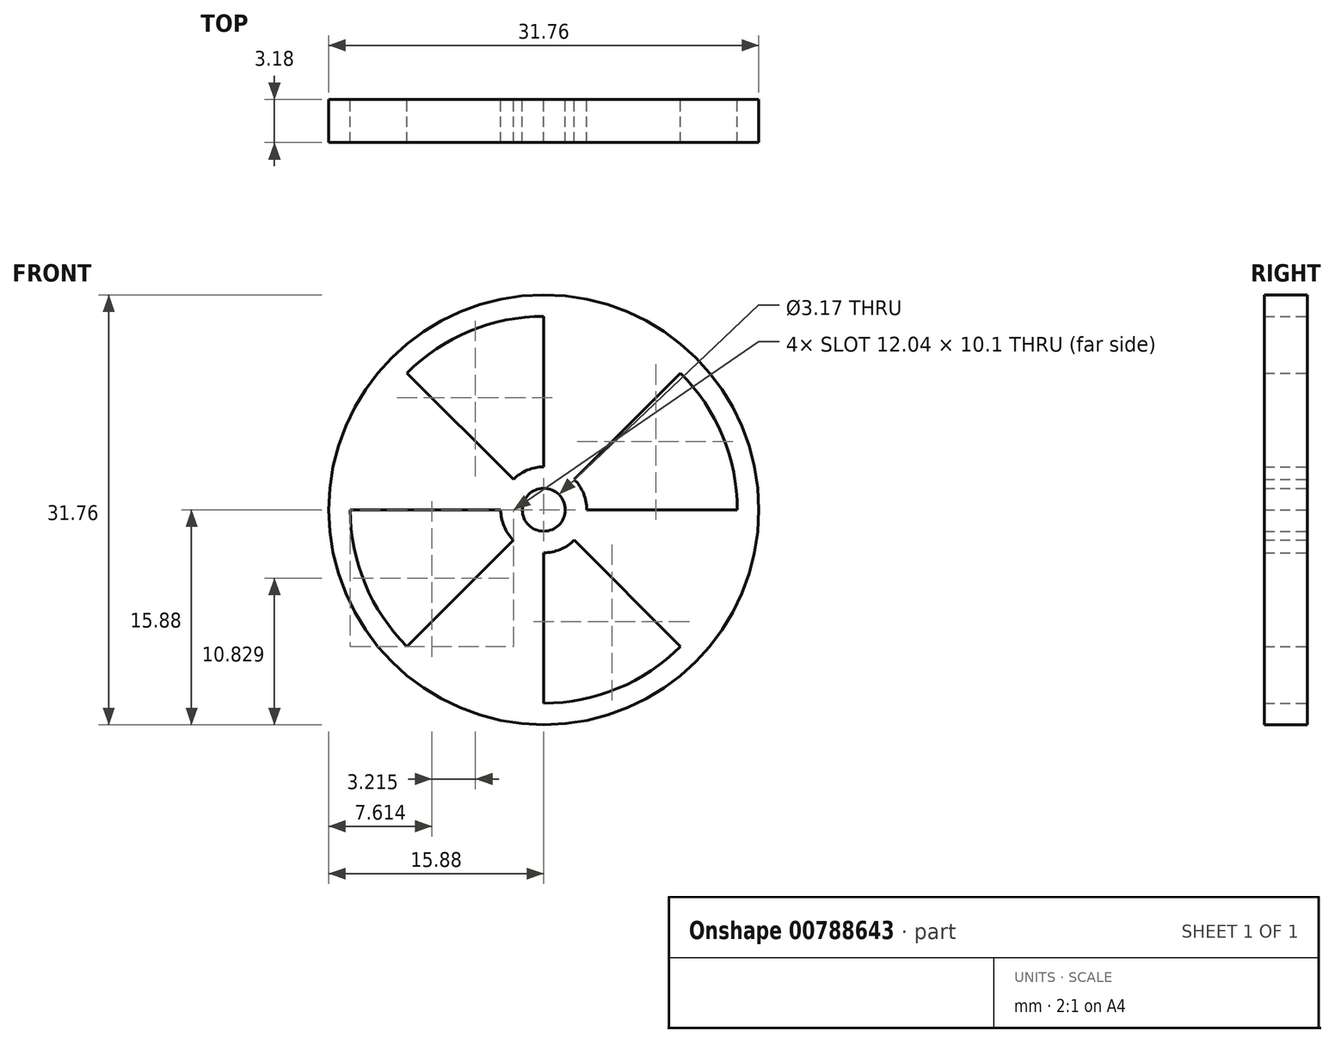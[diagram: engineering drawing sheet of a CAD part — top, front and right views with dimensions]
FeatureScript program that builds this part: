
annotation { "Feature Type Name" : "Feature", "Feature Type Description" : "" }
export const myFeature = defineFeature(function(context is Context, id is Id, definition is map)
    precondition{}
    {
        {
            var Q0;
            Q0=qCreatedBy(makeId("Front.planeOp"),FACE);
            var sketch = newSketch(context, id + "F0", { "sketchPlane" : qUnion([Q0])});
            skCircle(sketch, "E0", {"center": v(0, 0) * mm, "radius": 14.29 * mm});
            skCircle(sketch, "E1", {"center": v(0, 0) * mm, "radius": 3.18 * mm});
            skCircle(sketch, "E2", {"center": v(0, 0) * mm, "radius": 1.59 * mm});
            skCircle(sketch, "E3", {"center": v(0, 0) * mm, "radius": 15.88 * mm});
            skLineSegment(sketch, "E4", {"start": v(0, 3.18) * mm, "end": v(0, 14.29) * mm});
            skLineSegment(sketch, "E5", {"start": v(2.25, 2.25) * mm, "end": v(10.1, 10.1) * mm});
            skLineSegment(sketch, "E6.1.0", {"start": v(-3.18, 0) * mm, "end": v(-14.29, 0) * mm});
            skLineSegment(sketch, "E6.2.0", {"start": v(0, -3.18) * mm, "end": v(0, -14.29) * mm});
            skLineSegment(sketch, "E6.2.1", {"start": v(-2.25, -2.25) * mm, "end": v(-10.1, -10.1) * mm});
            skLineSegment(sketch, "E6.3.0", {"start": v(3.18, 0) * mm, "end": v(14.29, 0) * mm});
            skLineSegment(sketch, "E6.3.1", {"start": v(2.25, -2.25) * mm, "end": v(10.1, -10.1) * mm});
            skLineSegment(sketch, "E7.trimOffspring", {"start": v(-2.25, 2.25) * mm, "end": v(-10.1, 10.1) * mm});
            skSolve(sketch);
        }
        {
            var Q0;
            Q0 = qSketchRegion(id + "F0", true);
            var Q1;
            {var subQ0=sQuery(id+"F0.wireOp",EDGE,"E4");Q1=makeQuery(id+"F0.imprint","IMPRINT",FACE,{"disambiguationData":[TD([[makeQuery(id+"F0.imprint","IMPRINT",EDGE,{"derivedFrom":subQ0}),-1.0]])]});}
            var Q2;
            {var subQ0=sQuery(id+"F0.wireOp",EDGE,"E6.3.0");Q2=makeQuery(id+"F0.imprint","IMPRINT",FACE,{"disambiguationData":[TD([[makeQuery(id+"F0.imprint","IMPRINT",EDGE,{"derivedFrom":subQ0}),-1.0]])]});}
            var Q3;
            {var subQ0=sQuery(id+"F0.wireOp",EDGE,"E6.2.0");Q3=makeQuery(id+"F0.imprint","IMPRINT",FACE,{"disambiguationData":[TD([[makeQuery(id+"F0.imprint","IMPRINT",EDGE,{"derivedFrom":subQ0}),-1.0]])]});}
            var Q4;
            {var subQ0=sQuery(id+"F0.wireOp",EDGE,"E6.1.0");Q4=makeQuery(id+"F0.imprint","IMPRINT",FACE,{"disambiguationData":[TD([[makeQuery(id+"F0.imprint","IMPRINT",EDGE,{"derivedFrom":subQ0}),-1.0]])]});}
            var Q5;
            Q5=makeQuery(id+"F0.imprint","IMPRINT",FACE,{"disambiguationData":[TD([[makeQuery(id+"F0.imprint","IMPRINT",EDGE,{"derivedFrom":sQuery(id+"F0.wireOp",EDGE,"E2")}),-1.0]])]});
            extrude(context, id + "F1", {"entities" : qUnion([Q0, Q1, Q2, Q3, Q4, Q5]), "depth" : 3.17 * mm, "offsetDistance" : 25.4 * mm});
        }
    });
